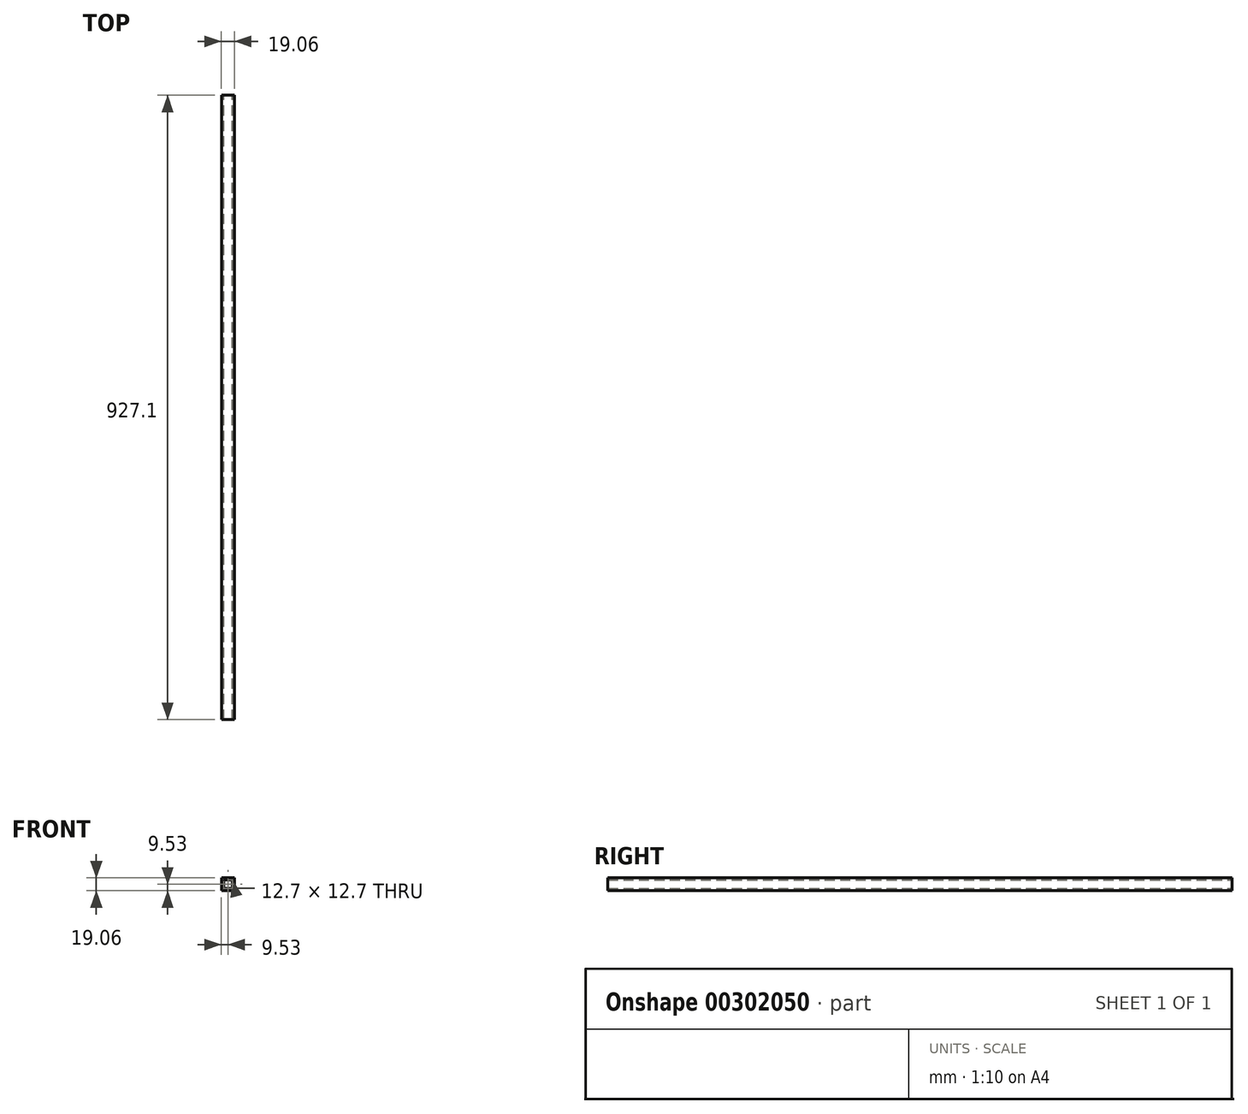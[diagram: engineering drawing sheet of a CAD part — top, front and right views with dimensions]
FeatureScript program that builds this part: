
annotation { "Feature Type Name" : "Feature", "Feature Type Description" : "" }
export const myFeature = defineFeature(function(context is Context, id is Id, definition is map)
    precondition{}
    {
        {
            var Q0;
            Q0=qCreatedBy(makeId("Front.planeOp"),FACE);
            var sketch = newSketch(context, id + "F0", { "sketchPlane" : qUnion([Q0])});
            skLineSegment(sketch, "E0.bottom", {"start": v(9.52, 9.53) * mm, "end": v(-9.53, 9.52) * mm});
            skLineSegment(sketch, "E0.top", {"start": v(9.53, -9.52) * mm, "end": v(-9.52, -9.53) * mm});
            skLineSegment(sketch, "E0.left", {"start": v(9.52, 9.53) * mm, "end": v(9.53, -9.52) * mm});
            skLineSegment(sketch, "E0.right", {"start": v(-9.53, 9.52) * mm, "end": v(-9.52, -9.53) * mm});
            skPoint(sketch, "E0.middle", {"position": v(0, 0) * mm});
            skLineSegment(sketch, "E1.bottom", {"start": v(6.35, 6.35) * mm, "end": v(-6.35, 6.35) * mm});
            skLineSegment(sketch, "E1.top", {"start": v(6.35, -6.35) * mm, "end": v(-6.35, -6.35) * mm});
            skLineSegment(sketch, "E1.left", {"start": v(6.35, 6.35) * mm, "end": v(6.35, -6.35) * mm});
            skLineSegment(sketch, "E1.right", {"start": v(-6.35, 6.35) * mm, "end": v(-6.35, -6.35) * mm});
            skSolve(sketch);
        }
        {
            var Q0;
            Q0 = qSketchRegion(id + "F0", true);
            extrude(context, id + "F1", {"entities" : qUnion([Q0]), "depth" : 927.1 * mm});
        }
    });
